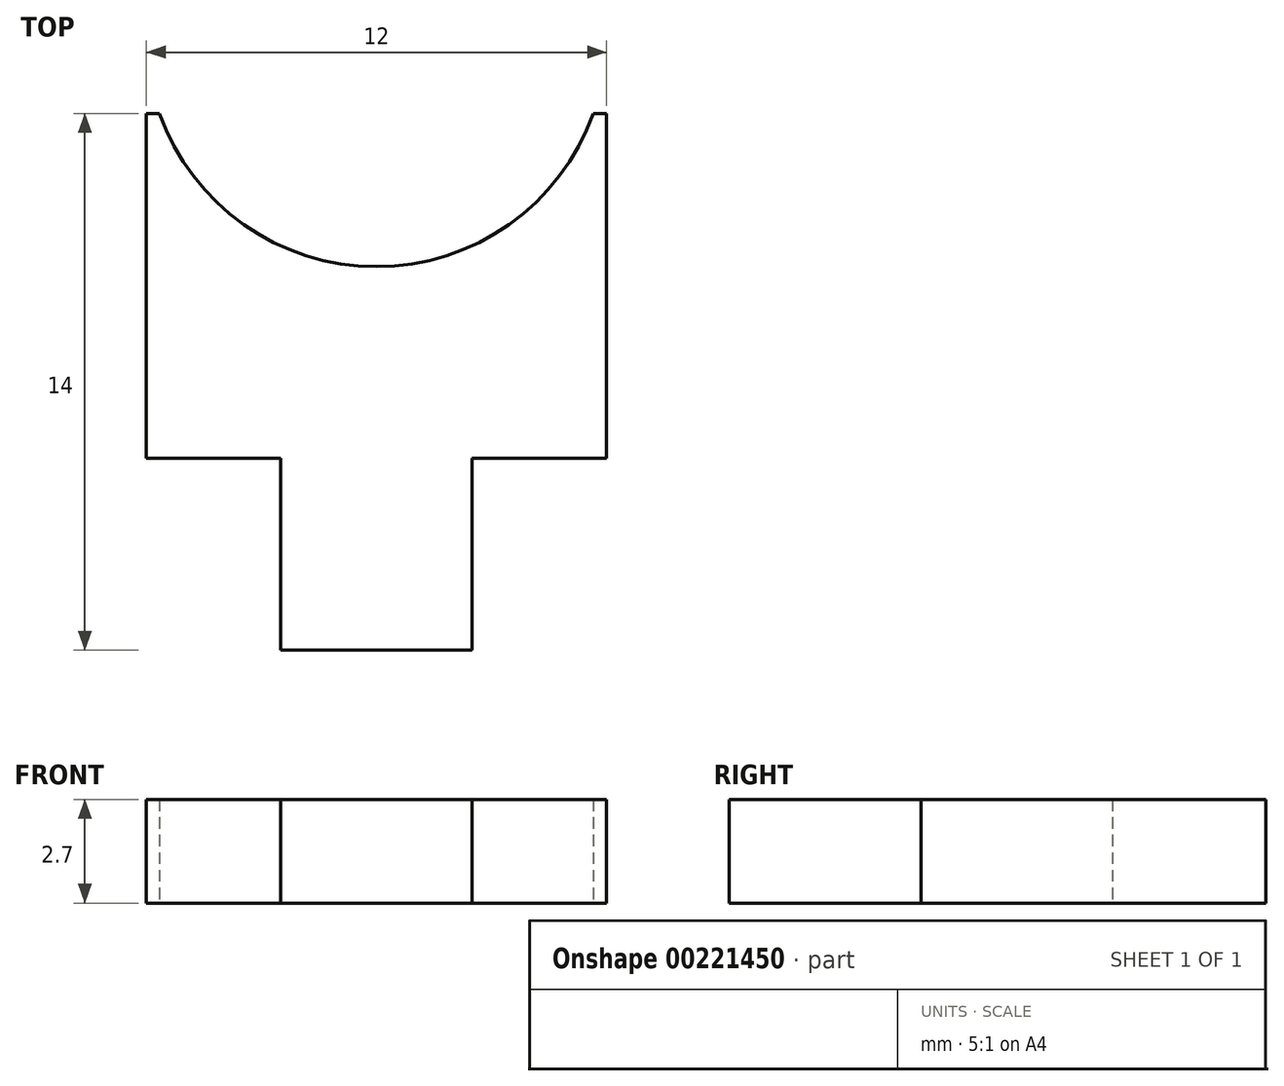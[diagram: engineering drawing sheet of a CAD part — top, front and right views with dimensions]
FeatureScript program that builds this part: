
annotation { "Feature Type Name" : "Feature", "Feature Type Description" : "" }
export const myFeature = defineFeature(function(context is Context, id is Id, definition is map)
    precondition{}
    {
        {
            var Q0;
            Q0=qCreatedBy(makeId("Top.planeOp"),FACE);
            var sketch = newSketch(context, id + "F0", { "sketchPlane" : qUnion([Q0])});
            skLineSegment(sketch, "E0.bottom", {"start": v(6, 4.5) * mm, "end": v(5.66, 4.5) * mm});
            skLineSegment(sketch, "E0.top", {"start": v(6, -4.5) * mm, "end": v(-6, -4.5) * mm});
            skLineSegment(sketch, "E0.left", {"start": v(6, 4.5) * mm, "end": v(6, -4.5) * mm});
            skLineSegment(sketch, "E0.right", {"start": v(-6, 4.5) * mm, "end": v(-6, -4.5) * mm});
            skPoint(sketch, "E0.middle", {"position": v(0, 0) * mm});
            skLineSegment(sketch, "E1", {"start": v(-6, 6.5) * mm, "end": v(6, 6.5) * mm, "construction": true});
            skArc(sketch, "E2", {"start": v(-5.66, 4.5) * mm, "mid": v(0, 0.5) * mm, "end": v(5.66, 4.5) * mm});
            skLineSegment(sketch, "E3.trimOffspring", {"start": v(-5.66, 4.5) * mm, "end": v(-6, 4.5) * mm});
            skLineSegment(sketch, "E4", {"start": v(-2.5, -4.5) * mm, "end": v(-2.5, -9.5) * mm});
            skLineSegment(sketch, "E5", {"start": v(-2.5, -9.5) * mm, "end": v(2.5, -9.5) * mm});
            skLineSegment(sketch, "E6", {"start": v(2.5, -9.5) * mm, "end": v(2.5, -4.5) * mm});
            skPoint(sketch, "E7", {"position": v(0, -9.5) * mm});
            skSolve(sketch);
        }
        {
            var Q0;
            Q0 = qSketchRegion(id + "F0", true);
            extrude(context, id + "F1", {"entities" : qUnion([Q0]), "depth" : 2.7 * mm});
        }
    });
